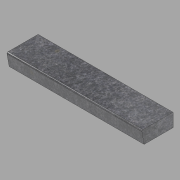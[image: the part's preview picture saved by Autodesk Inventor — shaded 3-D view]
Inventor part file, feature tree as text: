
AUTODESK INVENTOR PART (.ipt)
format: ipt  version: 2022.1 (Build 261234020, 234B)  size: 97,280 bytes
history: native  units: in
note: dims shown in document units (in); Inventor stores cm internally (conversion verified against a paired STEP export)
features: other x3, extrude x1, sketch x1
ambient origin geometry x8: Origin, YZ Plane, XZ Plane, XY Plane, X Axis, Y Axis, Z Axis, Center Point
bodies: Solid1 (feature_tree)
feature tree (5):
  other  "Blocks"
  extrude  "Extrusion1"  Depth=60.6875in TaperAngle=0.0deg
  sketch  "Sketch1"  dims[d0=13.0in d1=6.0in d2=13.5in d3=0.5in d4=0.5in d5=60.6875in d6=0.0in]
  other  "Profile"
  other  "Profile:1"
